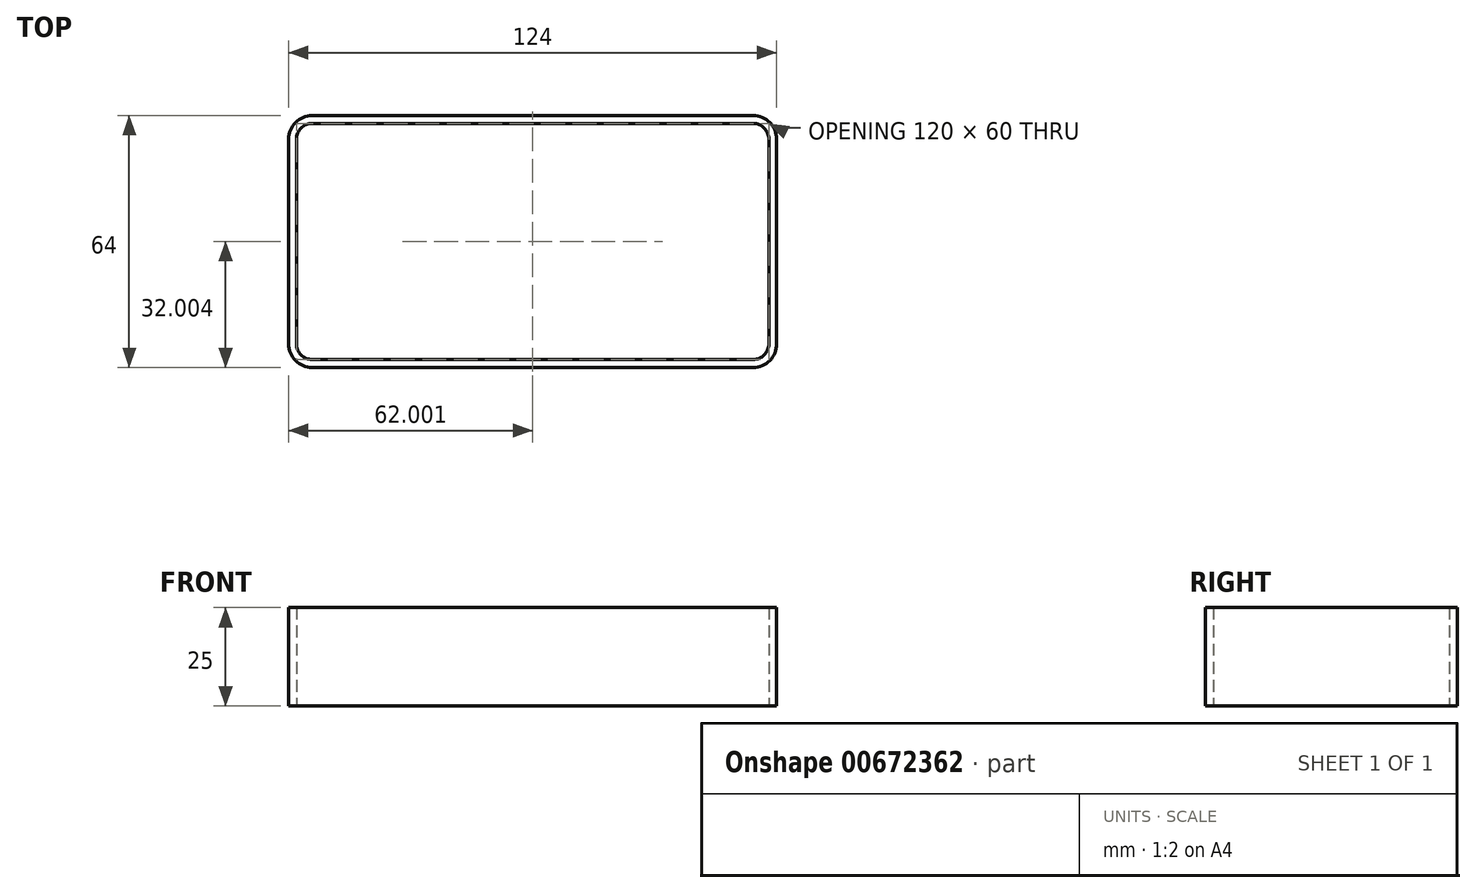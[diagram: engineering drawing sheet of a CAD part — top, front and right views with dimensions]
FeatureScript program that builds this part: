
annotation { "Feature Type Name" : "Feature", "Feature Type Description" : "" }
export const myFeature = defineFeature(function(context is Context, id is Id, definition is map)
    precondition{}
    {
        {
            var Q0;
            Q0=qCreatedBy(makeId("Top.planeOp"),FACE);
            var sketch = newSketch(context, id + "F0", { "sketchPlane" : qUnion([Q0])});
            skLineSegment(sketch, "E0.bottom", {"start": v(-56.05, 31.98) * mm, "end": v(55.95, 31.98) * mm});
            skLineSegment(sketch, "E0.top", {"start": v(-56.05, -32.02) * mm, "end": v(55.95, -32.02) * mm});
            skLineSegment(sketch, "E0.left", {"start": v(-62.05, 25.98) * mm, "end": v(-62.05, -26.02) * mm});
            skLineSegment(sketch, "E0.right", {"start": v(61.95, 25.98) * mm, "end": v(61.95, -26.02) * mm});
            skPoint(sketch, "E1.visualSharp", {"position": v(-62.05, 31.98) * mm});
            skArc(sketch, "E1.filletArc", {"start": v(-56.05, 31.98) * mm, "mid": v(-60.3, 30.23) * mm, "end": v(-62.05, 25.98) * mm});
            skPoint(sketch, "E2.visualSharp", {"position": v(61.95, 31.98) * mm});
            skArc(sketch, "E2.filletArc", {"start": v(61.95, 25.98) * mm, "mid": v(60.2, 30.23) * mm, "end": v(55.95, 31.98) * mm});
            skPoint(sketch, "E3.visualSharp", {"position": v(61.95, -32.02) * mm});
            skArc(sketch, "E3.filletArc", {"start": v(55.95, -32.02) * mm, "mid": v(60.2, -30.26) * mm, "end": v(61.95, -26.02) * mm});
            skPoint(sketch, "E4.visualSharp", {"position": v(-62.05, -32.02) * mm});
            skArc(sketch, "E4.filletArc", {"start": v(-62.05, -26.02) * mm, "mid": v(-60.3, -30.26) * mm, "end": v(-56.05, -32.02) * mm});
            skPoint(sketch, "E5", {"position": v(-0.05, -0.02) * mm});
            skArc(sketch, "E6.0", {"start": v(59.95, 25.98) * mm, "mid": v(58.78, 28.81) * mm, "end": v(55.95, 29.98) * mm});
            skLineSegment(sketch, "E6.1", {"start": v(-56.05, 29.98) * mm, "end": v(55.95, 29.98) * mm});
            skLineSegment(sketch, "E6.2", {"start": v(59.95, 25.98) * mm, "end": v(59.95, -26.02) * mm});
            skArc(sketch, "E6.3", {"start": v(-56.05, 29.98) * mm, "mid": v(-58.88, 28.81) * mm, "end": v(-60.05, 25.98) * mm});
            skArc(sketch, "E6.4", {"start": v(55.95, -30.02) * mm, "mid": v(58.78, -28.84) * mm, "end": v(59.95, -26.02) * mm});
            skLineSegment(sketch, "E6.5", {"start": v(-56.05, -30.02) * mm, "end": v(55.95, -30.02) * mm});
            skArc(sketch, "E6.6", {"start": v(-60.05, -26.02) * mm, "mid": v(-58.88, -28.84) * mm, "end": v(-56.05, -30.02) * mm});
            skLineSegment(sketch, "E6.7", {"start": v(-60.05, 25.98) * mm, "end": v(-60.05, -26.02) * mm});
            skSolve(sketch);
        }
        {
            var Q0;
            Q0=makeQuery(id+"F0.imprint","IMPRINT",FACE,{"disambiguationData":[TD([[makeQuery(id+"F0.imprint","IMPRINT",EDGE,{"derivedFrom":sQuery(id+"F0.wireOp",EDGE,"E0.bottom")}),-1.0]])]});
            extrude(context, id + "F1", {"entities" : qUnion([Q0]), "depth" : 25 * mm, "offsetDistance" : 25 * mm});
        }
    });
